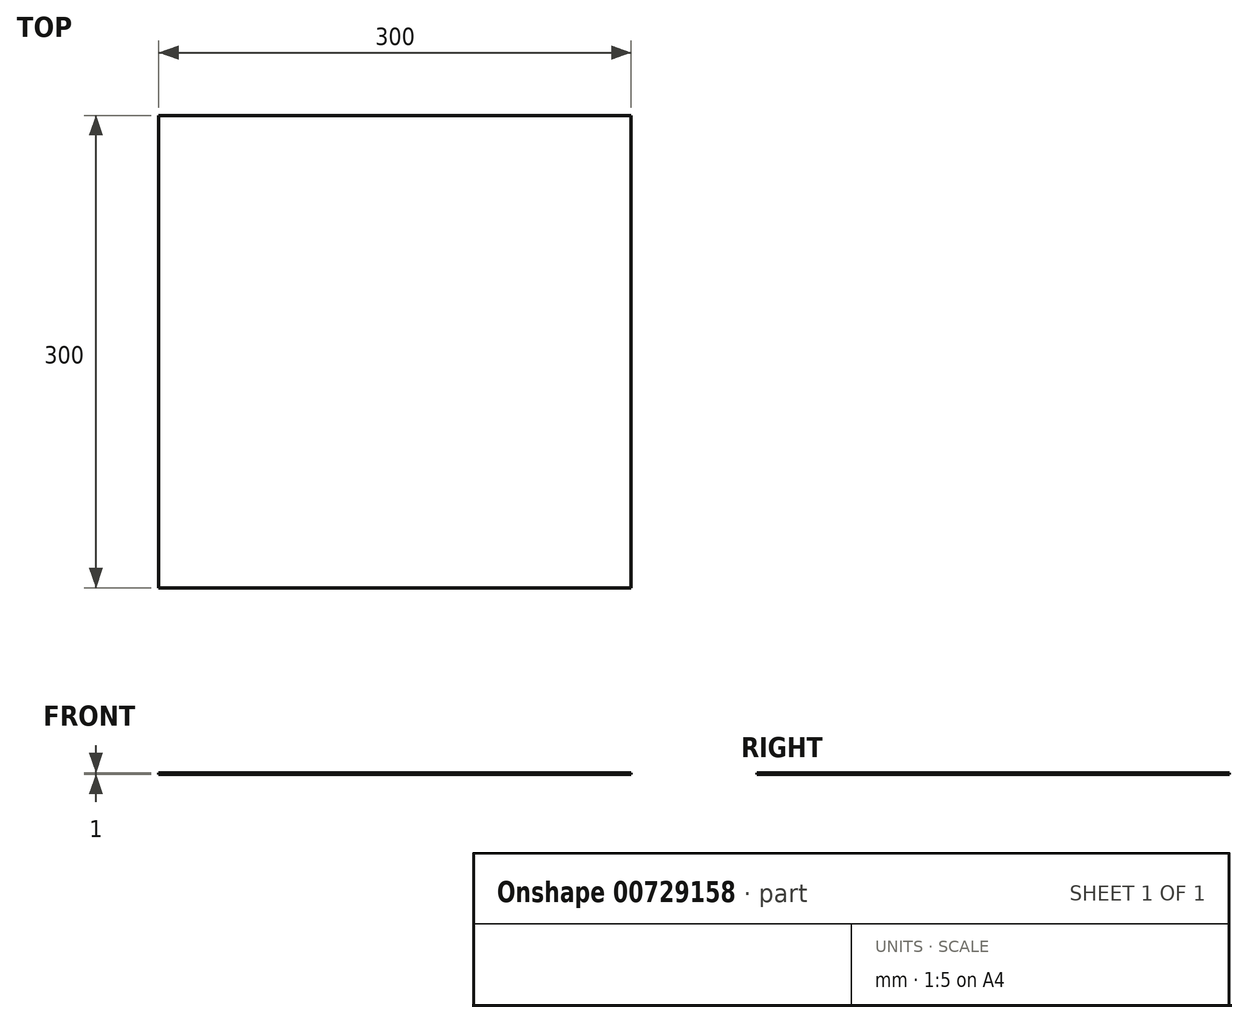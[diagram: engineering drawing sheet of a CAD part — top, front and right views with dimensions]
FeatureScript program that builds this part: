
annotation { "Feature Type Name" : "Feature", "Feature Type Description" : "" }
export const myFeature = defineFeature(function(context is Context, id is Id, definition is map)
    precondition{}
    {
        {
            var Q0;
            Q0=qCreatedBy(makeId("Top.planeOp"),FACE);
            var sketch = newSketch(context, id + "F0", { "sketchPlane" : qUnion([Q0])});
            skLineSegment(sketch, "E0.bottom", {"start": v(150, -150) * mm, "end": v(-150, -150) * mm});
            skLineSegment(sketch, "E0.top", {"start": v(150, 150) * mm, "end": v(-150, 150) * mm});
            skLineSegment(sketch, "E0.left", {"start": v(150, -150) * mm, "end": v(150, 150) * mm});
            skLineSegment(sketch, "E0.right", {"start": v(-150, -150) * mm, "end": v(-150, 150) * mm});
            skPoint(sketch, "E0.middle", {"position": v(0, 0) * mm});
            skSolve(sketch);
        }
        {
            var Q0;
            Q0=makeQuery(id+"F0.imprint","IMPRINT",FACE,{"disambiguationData":[TD([[makeQuery(id+"F0.imprint","IMPRINT",EDGE,{"derivedFrom":sQuery(id+"F0.wireOp",EDGE,"E0.bottom")}),-1.0]])]});
            extrude(context, id + "F1", {"entities" : qUnion([Q0]), "depth" : 1 * mm, "offsetDistance" : 25 * mm});
        }
    });
